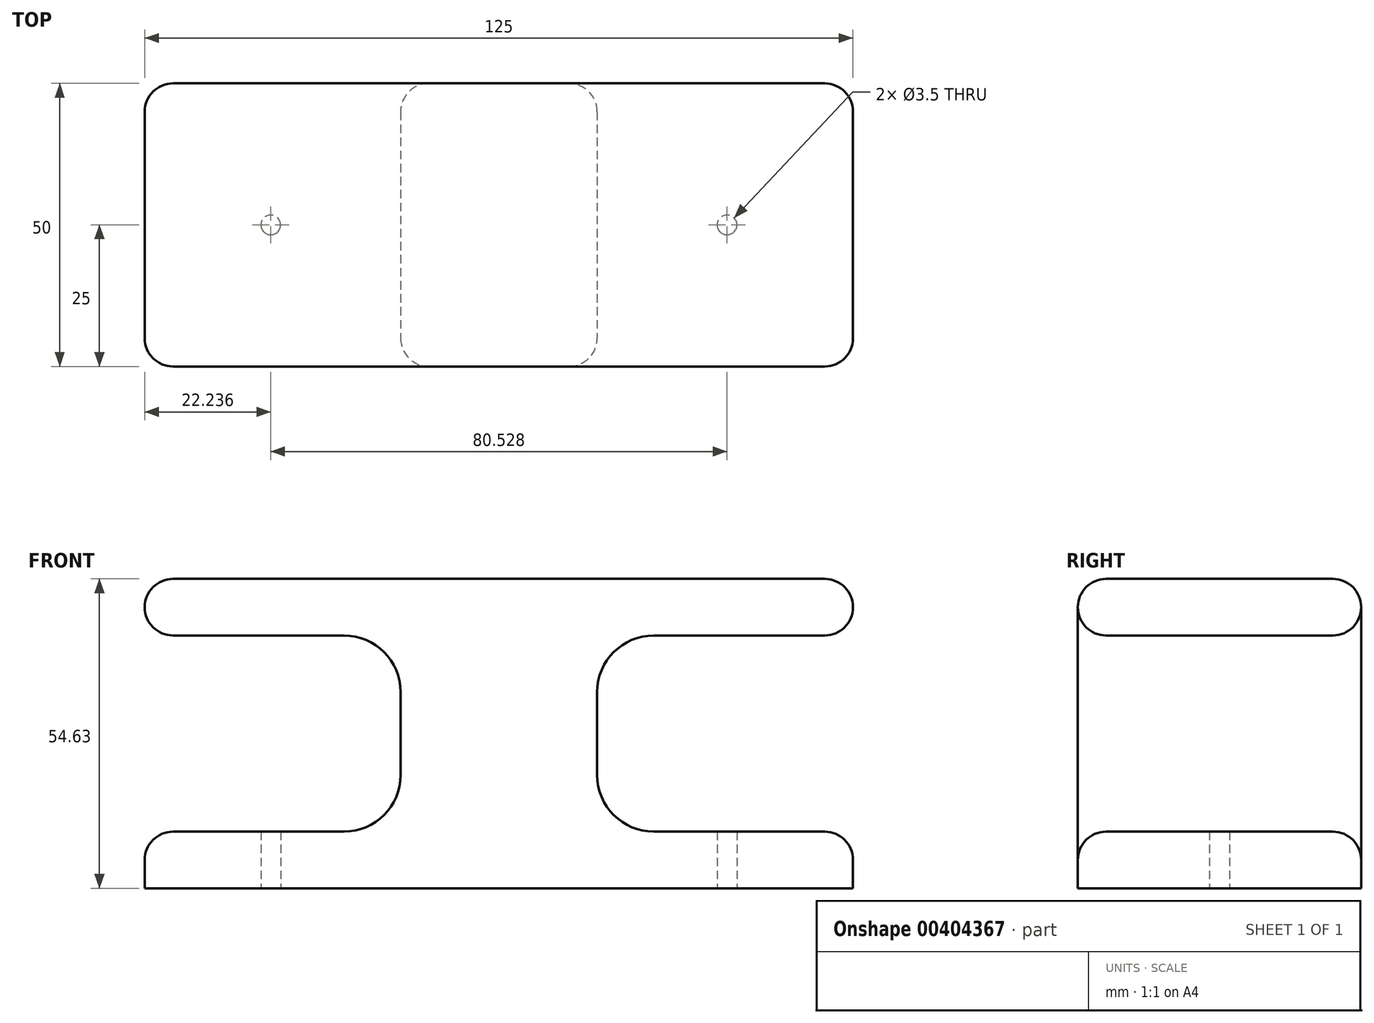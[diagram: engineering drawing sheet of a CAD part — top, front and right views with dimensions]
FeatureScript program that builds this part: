
annotation { "Feature Type Name" : "Feature", "Feature Type Description" : "" }
export const myFeature = defineFeature(function(context is Context, id is Id, definition is map)
    precondition{}
    {
        {
            var Q0;
            Q0=qCreatedBy(makeId("Top.planeOp"),FACE);
            var sketch = newSketch(context, id + "F0", { "sketchPlane" : qUnion([Q0])});
            skLineSegment(sketch, "E0.bottom", {"start": v(62.5, 25) * mm, "end": v(-62.5, 25) * mm});
            skLineSegment(sketch, "E0.top", {"start": v(62.5, -25) * mm, "end": v(-62.5, -25) * mm});
            skLineSegment(sketch, "E0.left", {"start": v(62.5, 25) * mm, "end": v(62.5, -25) * mm});
            skLineSegment(sketch, "E0.right", {"start": v(-62.5, 25) * mm, "end": v(-62.5, -25) * mm});
            skPoint(sketch, "E0.middle", {"position": v(0, 0) * mm});
            skLineSegment(sketch, "E1.bottom", {"start": v(-17.34, -25) * mm, "end": v(17.34, -25) * mm});
            skLineSegment(sketch, "E1.top", {"start": v(-17.34, 25) * mm, "end": v(17.34, 25) * mm});
            skLineSegment(sketch, "E1.left", {"start": v(-17.34, -25) * mm, "end": v(-17.34, 25) * mm});
            skLineSegment(sketch, "E1.right", {"start": v(17.34, -25) * mm, "end": v(17.34, 25) * mm});
            skLineSegment(sketch, "E2.bottom", {"start": v(-40.26, -25) * mm, "end": v(40.26, -25) * mm});
            skLineSegment(sketch, "E2.top", {"start": v(-40.26, 25) * mm, "end": v(40.26, 25) * mm});
            skPoint(sketch, "E3", {"position": v(-40.26, 0) * mm});
            skPoint(sketch, "E4", {"position": v(40.26, 0) * mm});
            skSolve(sketch);
        }
        {
            var Q0;
            {var subQ0=sQuery(id+"F0.wireOp",EDGE,"E0.right");Q0=makeQuery(id+"F0.imprint","IMPRINT",FACE,{"disambiguationData":[TD([[makeQuery(id+"F0.imprint","IMPRINT",EDGE,{"derivedFrom":subQ0}),1.0]])]});}
            var Q1;
            {var subQ0=sQuery(id+"F0.wireOp",EDGE,"E0.left");Q1=makeQuery(id+"F0.imprint","IMPRINT",FACE,{"disambiguationData":[TD([[makeQuery(id+"F0.imprint","IMPRINT",EDGE,{"derivedFrom":subQ0}),-1.0]])]});}
            var Q2;
            {var subQ0=sQuery(id+"F0.wireOp",EDGE,"E1.right");Q2=makeQuery(id+"F0.imprint","IMPRINT",FACE,{"disambiguationData":[TD([[makeQuery(id+"F0.imprint","IMPRINT",EDGE,{"derivedFrom":subQ0}),-1.0]])]});}
            var Q3;
            {var subQ0=sQuery(id+"F0.wireOp",EDGE,"E1.left");Q3=makeQuery(id+"F0.imprint","IMPRINT",FACE,{"disambiguationData":[TD([[makeQuery(id+"F0.imprint","IMPRINT",EDGE,{"derivedFrom":subQ0}),-1.0]])]});}
            var Q4;
            {var subQ0=sQuery(id+"F0.wireOp",EDGE,"E1.left");Q4=makeQuery(id+"F0.imprint","IMPRINT",FACE,{"disambiguationData":[TD([[makeQuery(id+"F0.imprint","IMPRINT",EDGE,{"derivedFrom":subQ0}),1.0]])]});}
            extrude(context, id + "F1", {"entities" : qUnion([Q0, Q1, Q2, Q3, Q4]), "depth" : 10 * mm});
        }
        {
            var Q0;
            {var subQ0=sQuery(id+"F0.wireOp",EDGE,"E1.left");Q0=makeQuery(id+"F0.imprint","IMPRINT",FACE,{"disambiguationData":[TD([[makeQuery(id+"F0.imprint","IMPRINT",EDGE,{"derivedFrom":subQ0}),-1.0]])]});}
            extrude(context, id + "F2", {"entities" : qUnion([Q0]), "operationType" : NewBodyOperationType.ADD, "depth" : 50 * mm});
        }
        {
            var Q0;
            Q0=qCreatedBy(makeId("Front.planeOp"),FACE);
            var sketch = newSketch(context, id + "F3", { "sketchPlane" : qUnion([Q0])});
            skLineSegment(sketch, "E5.bottom", {"start": v(62.5, 54.63) * mm, "end": v(-62.5, 54.63) * mm});
            skLineSegment(sketch, "E5.top", {"start": v(62.5, 44.63) * mm, "end": v(-62.5, 44.63) * mm});
            skLineSegment(sketch, "E5.left", {"start": v(62.5, 54.63) * mm, "end": v(62.5, 44.63) * mm});
            skLineSegment(sketch, "E5.right", {"start": v(-62.5, 54.63) * mm, "end": v(-62.5, 44.63) * mm});
            skPoint(sketch, "E5.middle", {"position": v(0, 49.63) * mm});
            skSolve(sketch);
        }
        {
            var Q0;
            Q0=makeQuery(id+"F3.imprint","IMPRINT",FACE,{"disambiguationData":[TD([[makeQuery(id+"F3.imprint","IMPRINT",EDGE,{"derivedFrom":sQuery(id+"F3.wireOp",EDGE,"E5.bottom")}),1.0]])]});
            extrude(context, id + "F4", {"entities" : qUnion([Q0]), "operationType" : NewBodyOperationType.ADD, "endBound" : BoundingType.SYMMETRIC, "depth" : 50 * mm});
        }
        {
            var Q0;
            Q0=makeQuery(id+"F2.boolean.opBoolean","INTERSECT",EDGE,{"derivedFrom":[makeQuery(id+"F1.opExtrude","CAP_FACE",FACE,{"disambiguationData":[OSD([sQuery(id+"F0.wireOp",EDGE,"E0.bottom"),sQuery(id+"F0.wireOp",EDGE,"E0.top"),sQuery(id+"F0.wireOp",EDGE,"E0.left"),sQuery(id+"F0.wireOp",EDGE,"E0.right"),sQuery(id+"F0.wireOp",EDGE,"E2.bottom"),sQuery(id+"F0.wireOp",EDGE,"E2.top")])],"isStart":false}),makeQuery(id+"F2.opExtrude","SWEPT_FACE",FACE,{"disambiguationData":[OSD([sQuery(id+"F0.wireOp",EDGE,"E1.left")])]})]});
            var Q1;
            Q1=makeQuery(id+"F2.boolean.opBoolean","INTERSECT",EDGE,{"derivedFrom":[makeQuery(id+"F1.opExtrude","CAP_FACE",FACE,{"disambiguationData":[OSD([sQuery(id+"F0.wireOp",EDGE,"E0.bottom"),sQuery(id+"F0.wireOp",EDGE,"E0.top"),sQuery(id+"F0.wireOp",EDGE,"E0.left"),sQuery(id+"F0.wireOp",EDGE,"E0.right"),sQuery(id+"F0.wireOp",EDGE,"E2.bottom"),sQuery(id+"F0.wireOp",EDGE,"E2.top")])],"isStart":false}),makeQuery(id+"F2.opExtrude","SWEPT_FACE",FACE,{"disambiguationData":[OSD([sQuery(id+"F0.wireOp",EDGE,"E1.right")])]})]});
            var Q2;
            Q2=makeQuery(id+"F4.boolean.opBoolean","INTERSECT",EDGE,{"derivedFrom":[makeQuery(id+"F2.opExtrude","SWEPT_FACE",FACE,{"disambiguationData":[OSD([sQuery(id+"F0.wireOp",EDGE,"E1.right")])]}),makeQuery(id+"F4.opExtrude","SWEPT_FACE",FACE,{"disambiguationData":[OSD([sQuery(id+"F3.wireOp",EDGE,"E5.top")])]})]});
            var Q3;
            Q3=makeQuery(id+"F4.boolean.opBoolean","INTERSECT",EDGE,{"derivedFrom":[makeQuery(id+"F2.opExtrude","SWEPT_FACE",FACE,{"disambiguationData":[OSD([sQuery(id+"F0.wireOp",EDGE,"E1.left")])]}),makeQuery(id+"F4.opExtrude","SWEPT_FACE",FACE,{"disambiguationData":[OSD([sQuery(id+"F3.wireOp",EDGE,"E5.top")])]})]});
            fillet(context, id + "F5", {"entities" : qUnion([Q0, Q1, Q2, Q3]), "radius" : 10 * mm, "tangentPropagation" : true, "allowEdgeOverflow" : false});
        }
        {
            var Q0;
            {var subQ0=sQuery(id+"F0.wireOp",EDGE,"E0.left");var subQ1=sQuery(id+"F0.wireOp",EDGE,"E2.bottom");var subQ2=sQuery(id+"F0.wireOp",EDGE,"E0.top");Q0=makeQuery(id+"F2.boolean.opBoolean","SPLIT",EDGE,{"disambiguationData":[TD([makeQuery(id+"F1.opExtrude","SWEPT_FACE",FACE,{"disambiguationData":[OSD([subQ0])]})])],"derivedFrom":makeQuery(id+"F1.opExtrude","CAP_EDGE",EDGE,{"disambiguationData":[OSD([subQ2,subQ1])],"isStart":false})});}
            var Q1;
            {var subQ0=sQuery(id+"F0.wireOp",EDGE,"E0.left");var subQ1=sQuery(id+"F0.wireOp",EDGE,"E2.top");var subQ2=sQuery(id+"F0.wireOp",EDGE,"E0.bottom");Q1=makeQuery(id+"F2.boolean.opBoolean","SPLIT",EDGE,{"disambiguationData":[TD([makeQuery(id+"F1.opExtrude","SWEPT_FACE",FACE,{"disambiguationData":[OSD([subQ0])]})])],"derivedFrom":makeQuery(id+"F1.opExtrude","CAP_EDGE",EDGE,{"disambiguationData":[OSD([subQ2,subQ1])],"isStart":false})});}
            var Q2;
            {var subQ0=sQuery(id+"F0.wireOp",EDGE,"E0.right");var subQ1=sQuery(id+"F0.wireOp",EDGE,"E2.bottom");var subQ2=sQuery(id+"F0.wireOp",EDGE,"E0.top");Q2=makeQuery(id+"F2.boolean.opBoolean","SPLIT",EDGE,{"disambiguationData":[TD([makeQuery(id+"F1.opExtrude","SWEPT_FACE",FACE,{"disambiguationData":[OSD([subQ0])]})])],"derivedFrom":makeQuery(id+"F1.opExtrude","CAP_EDGE",EDGE,{"disambiguationData":[OSD([subQ2,subQ1])],"isStart":false})});}
            var Q3;
            {var subQ0=sQuery(id+"F0.wireOp",EDGE,"E0.right");var subQ1=sQuery(id+"F0.wireOp",EDGE,"E2.top");var subQ2=sQuery(id+"F0.wireOp",EDGE,"E0.bottom");Q3=makeQuery(id+"F2.boolean.opBoolean","SPLIT",EDGE,{"disambiguationData":[TD([makeQuery(id+"F1.opExtrude","SWEPT_FACE",FACE,{"disambiguationData":[OSD([subQ0])]})])],"derivedFrom":makeQuery(id+"F1.opExtrude","CAP_EDGE",EDGE,{"disambiguationData":[OSD([subQ2,subQ1])],"isStart":false})});}
            fillet(context, id + "F6", {"entities" : qUnion([Q0, Q1, Q2, Q3]), "radius" : 5 * mm, "tangentPropagation" : true, "allowEdgeOverflow" : false});
        }
        {
            var Q0;
            Q0=makeQuery(id+"F1.opExtrude","CAP_EDGE",EDGE,{"disambiguationData":[OSD([sQuery(id+"F0.wireOp",EDGE,"E0.right")])],"isStart":false});
            var Q1;
            Q1=makeQuery(id+"F4.opExtrude","SWEPT_EDGE",EDGE,{"disambiguationData":[OSD([sQuery(id+"F3.wireOp",EDGE,"E5.top"),sQuery(id+"F3.wireOp",EDGE,"E5.right")])]});
            var Q2;
            Q2=makeQuery(id+"F1.opExtrude","CAP_EDGE",EDGE,{"disambiguationData":[OSD([sQuery(id+"F0.wireOp",EDGE,"E0.left")])],"isStart":false});
            var Q3;
            Q3=makeQuery(id+"F4.opExtrude","SWEPT_EDGE",EDGE,{"disambiguationData":[OSD([sQuery(id+"F3.wireOp",EDGE,"E5.top"),sQuery(id+"F3.wireOp",EDGE,"E5.left")])]});
            fillet(context, id + "F7", {"entities" : qUnion([Q0, Q1, Q2, Q3]), "radius" : 5 * mm, "tangentPropagation" : true, "allowEdgeOverflow" : false});
        }
        {
            var Q0;
            Q0=sQuery(id+"F0.wireOp",VERTEX,"E3");
            var Q1;
            Q1=sQuery(id+"F0.wireOp",VERTEX,"E4");
            var Q2;
            Q2=makeQuery(id+"F1.opExtrude","SWEPT_BODY",BODY,{"disambiguationData":[OSD([sQuery(id+"F0.wireOp",EDGE,"E0.bottom"),sQuery(id+"F0.wireOp",EDGE,"E0.top"),sQuery(id+"F0.wireOp",EDGE,"E0.left"),sQuery(id+"F0.wireOp",EDGE,"E0.right"),sQuery(id+"F0.wireOp",EDGE,"E2.bottom"),sQuery(id+"F0.wireOp",EDGE,"E2.top")])]});
            hole(context, id + "F8", {"style" : HoleStyle.SIMPLE, "endStyle" : HoleEndStyle.BLIND, "oppositeDirection" : true, "holeDiameter" : 3.5 * mm, "holeDepth" : 12 * mm, "isTappedThrough" : true, "tappedDepth" : 12 * mm, "tapClearance" : 3, "locations" : qUnion([Q0, Q1]), "scope" : qUnion([Q2])});
        }
        {
            var Q0;
            Q0=makeQuery(id+"F4.opExtrude","CAP_EDGE",EDGE,{"disambiguationData":[OSD([sQuery(id+"F3.wireOp",EDGE,"E5.bottom")])],"isStart":true});
            var Q1;
            Q1=makeQuery(id+"F4.opExtrude","SWEPT_EDGE",EDGE,{"disambiguationData":[OSD([sQuery(id+"F3.wireOp",EDGE,"E5.bottom"),sQuery(id+"F3.wireOp",EDGE,"E5.left")])]});
            fillet(context, id + "F9", {"entities" : qUnion([Q0, Q1]), "radius" : 5 * mm, "tangentPropagation" : true, "allowEdgeOverflow" : false});
        }
    });
